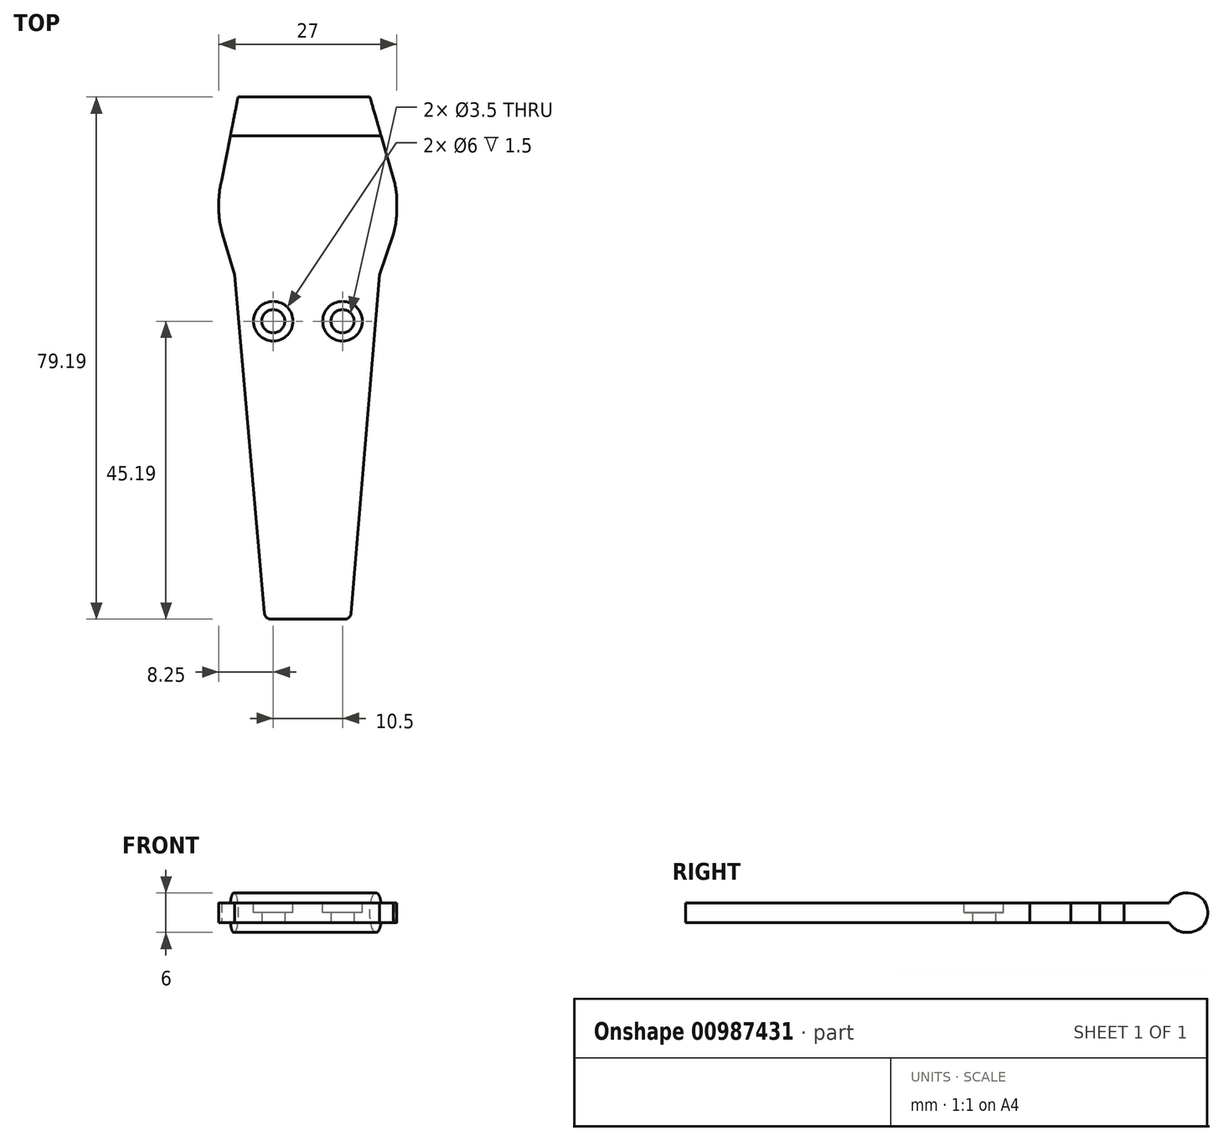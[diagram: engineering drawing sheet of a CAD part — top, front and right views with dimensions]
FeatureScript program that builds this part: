
annotation { "Feature Type Name" : "Feature", "Feature Type Description" : "" }
export const myFeature = defineFeature(function(context is Context, id is Id, definition is map)
    precondition{}
    {
        {
            var Q0;
            Q0=qCreatedBy(makeId("Top.planeOp"),FACE);
            var sketch = newSketch(context, id + "F0", { "sketchPlane" : qUnion([Q0])});
            skLineSegment(sketch, "E0.bottom", {"start": v(5.58, -42.2) * mm, "end": v(-5.58, -42.2) * mm});
            skPoint(sketch, "E0.middle", {"position": v(0, 0) * mm});
            skArc(sketch, "E1", {"start": v(-13.1, 24.3) * mm, "mid": v(-13.42, 22.46) * mm, "end": v(-13.5, 20.6) * mm});
            skLineSegment(sketch, "E2", {"start": v(-5.25, 37) * mm, "end": v(4.98, 37) * mm});
            skLineSegment(sketch, "E3", {"start": v(-10.8, 35.97) * mm, "end": v(-13.36, 22.92) * mm});
            skLineSegment(sketch, "E4", {"start": v(10.3, 33.9) * mm, "end": v(13.1, 24.27) * mm});
            skPoint(sketch, "E5.orphan", {"position": v(-13.5, 42.2) * mm});
            skPoint(sketch, "E6.orphan", {"position": v(13.5, 42.2) * mm});
            skPoint(sketch, "E7.visualSharp", {"position": v(-10.6, 37) * mm});
            skPoint(sketch, "E8.visualSharp", {"position": v(9.4, 37) * mm});
            skLineSegment(sketch, "E9", {"start": v(-0.13, 10) * mm, "end": v(25.95, 10) * mm, "construction": true});
            skLineSegment(sketch, "E10", {"start": v(-0.13, 10) * mm, "end": v(10.87, 10) * mm, "construction": true});
            skLineSegment(sketch, "E11", {"start": v(-0.13, 10) * mm, "end": v(-11.12, 10) * mm, "construction": true});
            skLineSegment(sketch, "E12", {"start": v(-13.5, 20.6) * mm, "end": v(-13.49, 20.58) * mm});
            skLineSegment(sketch, "E13", {"start": v(-6.58, -41.28) * mm, "end": v(-11.12, 10) * mm});
            skLineSegment(sketch, "E14", {"start": v(10.87, 10) * mm, "end": v(6.58, -41.28) * mm});
            skPoint(sketch, "E15.orphan", {"position": v(13.5, -42.2) * mm});
            skPoint(sketch, "E0.right.start.orphan", {"position": v(-13.5, -42.2) * mm});
            skArc(sketch, "E16.trimOffspring", {"start": v(13.5, 20.6) * mm, "mid": v(13.42, 22.45) * mm, "end": v(13.1, 24.27) * mm});
            skLineSegment(sketch, "E17", {"start": v(-0.13, 10) * mm, "end": v(-0.13, -32) * mm, "construction": true});
            skPoint(sketch, "E18.visualSharp", {"position": v(-6.5, -42.2) * mm});
            skArc(sketch, "E18.filletArc", {"start": v(-6.58, -41.28) * mm, "mid": v(-6.26, -41.93) * mm, "end": v(-5.58, -42.2) * mm});
            skPoint(sketch, "E19.visualSharp", {"position": v(6.5, -42.2) * mm});
            skArc(sketch, "E19.filletArc", {"start": v(5.58, -42.2) * mm, "mid": v(6.26, -41.93) * mm, "end": v(6.58, -41.28) * mm});
            skLineSegment(sketch, "E20", {"start": v(-10.8, 35.97) * mm, "end": v(-10.6, 37) * mm});
            skLineSegment(sketch, "E21", {"start": v(-10.6, 37) * mm, "end": v(-5.25, 37) * mm});
            skLineSegment(sketch, "E22", {"start": v(4.98, 37) * mm, "end": v(9.4, 37) * mm});
            skLineSegment(sketch, "E23", {"start": v(9.4, 37) * mm, "end": v(10.3, 33.9) * mm});
            skLineSegment(sketch, "E24", {"start": v(5.25, 0) * mm, "end": v(-5.25, 0) * mm, "construction": true});
            skLineSegment(sketch, "E25", {"start": v(17.3, 3) * mm, "end": v(-16.73, 3) * mm, "construction": true});
            skLineSegment(sketch, "E26", {"start": v(5.25, 0) * mm, "end": v(5.25, 8.34) * mm, "construction": true});
            skLineSegment(sketch, "E27", {"start": v(-5.25, 0) * mm, "end": v(-5.25, 8.21) * mm, "construction": true});
            skCircle(sketch, "E28", {"center": v(5.25, 3) * mm, "radius": 1.75 * mm});
            skCircle(sketch, "E29", {"center": v(-5.25, 3) * mm, "radius": 1.75 * mm});
            skLineSegment(sketch, "E30", {"start": v(0, 37) * mm, "end": v(0, 20) * mm, "construction": true});
            skArc(sketch, "E31", {"start": v(12.95, 16.18) * mm, "mid": v(13.4, 18.36) * mm, "end": v(13.49, 20.58) * mm});
            skLineSegment(sketch, "E32.trimOffspring", {"start": v(13.49, 20.58) * mm, "end": v(13.5, 20.6) * mm});
            skLineSegment(sketch, "E33", {"start": v(-11.12, 10) * mm, "end": v(-12.95, 16.18) * mm});
            skLineSegment(sketch, "E34", {"start": v(12.95, 16.18) * mm, "end": v(10.87, 10) * mm});
            skArc(sketch, "E35.trimOffspring", {"start": v(-13.49, 20.58) * mm, "mid": v(-13.4, 18.36) * mm, "end": v(-12.95, 16.18) * mm});
            skSolve(sketch);
        }
        {
            var Q0;
            Q0 = qSketchRegion(id + "F0", true);
            extrude(context, id + "F1", {"entities" : qUnion([Q0]), "depth" : 3 * mm, "offsetDistance" : 25 * mm});
        }
        {
            var Q0;
            Q0=makeQuery(id+"F1.opExtrude","CAP_FACE",FACE,{"disambiguationData":[OSD([sQuery(id+"F0.wireOp",EDGE,"E0.bottom"),sQuery(id+"F0.wireOp",EDGE,"E1"),sQuery(id+"F0.wireOp",EDGE,"E2"),sQuery(id+"F0.wireOp",EDGE,"E3"),sQuery(id+"F0.wireOp",EDGE,"E4"),sQuery(id+"F0.wireOp",EDGE,"pwRtYjBo-2US5-fapG-OBra-nsn0KMgqBpwr"),sQuery(id+"F0.wireOp",EDGE,"E12"),sQuery(id+"F0.wireOp",EDGE,"E13"),sQuery(id+"F0.wireOp",EDGE,"E14"),sQuery(id+"F0.wireOp",EDGE,"E16.trimOffspring"),sQuery(id+"F0.wireOp",EDGE,"E18.filletArc"),sQuery(id+"F0.wireOp",EDGE,"E19.filletArc"),sQuery(id+"F0.wireOp",EDGE,"E20"),sQuery(id+"F0.wireOp",EDGE,"E21"),sQuery(id+"F0.wireOp",EDGE,"E22"),sQuery(id+"F0.wireOp",EDGE,"E23")])],"isStart":false});
            var sketch = newSketch(context, id + "F2", { "sketchPlane" : qUnion([Q0])});
            skLineSegment(sketch, "E36", {"start": v(-10.6, 37) * mm, "end": v(-11.75, 31.11) * mm});
            skLineSegment(sketch, "E37", {"start": v(-11.75, 31.11) * mm, "end": v(11.12, 31.11) * mm});
            skLineSegment(sketch, "E38", {"start": v(11.12, 31.11) * mm, "end": v(9.4, 37) * mm});
            skLineSegment(sketch, "E39", {"start": v(9.4, 37) * mm, "end": v(-10.6, 37) * mm});
            skSolve(sketch);
        }
        {
            var Q0;
            Q0 = qSketchRegion(id + "F2", true);
            extrude(context, id + "F3", {"entities" : qUnion([Q0]), "operationType" : NewBodyOperationType.ADD, "depth" : 1.5 * mm, "offsetDistance" : 25 * mm, "hasSecondDirection" : true, "secondDirectionOppositeDirection" : true, "secondDirectionDepth" : 4.5 * mm});
        }
        {
            var Q0;
            Q0=makeQuery(id+"F3.opExtrude","CAP_EDGE",EDGE,{"disambiguationData":[OSD([sQuery(id+"F2.wireOp",EDGE,"W42PlOKo-ny84-9Naq-Bdwa-5Mfub0ToF7hg.bottom")])],"isStart":false});
            var Q1;
            Q1=makeQuery(id+"F3.opExtrude","CAP_EDGE",EDGE,{"disambiguationData":[OSD([sQuery(id+"F2.wireOp",EDGE,"E37")])],"isStart":false});
            var Q2;
            Q2=makeQuery(id+"F3.opExtrude","CAP_EDGE",EDGE,{"disambiguationData":[OSD([sQuery(id+"F2.wireOp",EDGE,"W42PlOKo-ny84-9Naq-Bdwa-5Mfub0ToF7hg.bottom")])],"isStart":true});
            var Q3;
            Q3=makeQuery(id+"F3.opExtrude","CAP_EDGE",EDGE,{"disambiguationData":[OSD([sQuery(id+"F2.wireOp",EDGE,"E37")])],"isStart":true});
            var Q4;
            Q4=makeQuery(id+"F3.opExtrude","CAP_EDGE",EDGE,{"disambiguationData":[OSD([sQuery(id+"F2.wireOp",EDGE,"E39")])],"isStart":false});
            var Q5;
            Q5=makeQuery(id+"F3.opExtrude","CAP_EDGE",EDGE,{"disambiguationData":[OSD([sQuery(id+"F2.wireOp",EDGE,"E39")])],"isStart":true});
            fillet(context, id + "F4", {"entities" : qUnion([Q0, Q1, Q2, Q3, Q4, Q5]), "radius" : 3 * mm, "tangentPropagation" : true, "allowEdgeOverflow" : false});
        }
        {
            var Q0;
            Q0=makeQuery(id+"F1.opExtrude","CAP_FACE",FACE,{"disambiguationData":[OSD([sQuery(id+"F0.wireOp",EDGE,"E0.bottom"),sQuery(id+"F0.wireOp",EDGE,"E1"),sQuery(id+"F0.wireOp",EDGE,"E2"),sQuery(id+"F0.wireOp",EDGE,"E3"),sQuery(id+"F0.wireOp",EDGE,"E4"),sQuery(id+"F0.wireOp",EDGE,"E12"),sQuery(id+"F0.wireOp",EDGE,"E13"),sQuery(id+"F0.wireOp",EDGE,"E14"),sQuery(id+"F0.wireOp",EDGE,"E16.trimOffspring"),sQuery(id+"F0.wireOp",EDGE,"E18.filletArc"),sQuery(id+"F0.wireOp",EDGE,"E19.filletArc"),sQuery(id+"F0.wireOp",EDGE,"E20"),sQuery(id+"F0.wireOp",EDGE,"E21"),sQuery(id+"F0.wireOp",EDGE,"E22"),sQuery(id+"F0.wireOp",EDGE,"E23"),sQuery(id+"F0.wireOp",EDGE,"E28"),sQuery(id+"F0.wireOp",EDGE,"E29"),sQuery(id+"F0.wireOp",EDGE,"E31"),sQuery(id+"F0.wireOp",EDGE,"E32.trimOffspring"),sQuery(id+"F0.wireOp",EDGE,"E33"),sQuery(id+"F0.wireOp",EDGE,"E34"),sQuery(id+"F0.wireOp",EDGE,"E35.trimOffspring")])],"isStart":false});
            var sketch = newSketch(context, id + "F5", { "sketchPlane" : qUnion([Q0])});
            skCircle(sketch, "E40", {"center": v(-5.25, 3) * mm, "radius": 3 * mm});
            skCircle(sketch, "E41", {"center": v(5.25, 3) * mm, "radius": 3 * mm});
            skSolve(sketch);
        }
        {
            var Q0;
            Q0 = qSketchRegion(id + "F5", true);
            extrude(context, id + "F6", {"entities" : qUnion([Q0]), "operationType" : NewBodyOperationType.REMOVE, "oppositeDirection" : true, "depth" : 1.5 * mm, "offsetDistance" : 25 * mm});
        }
    });
